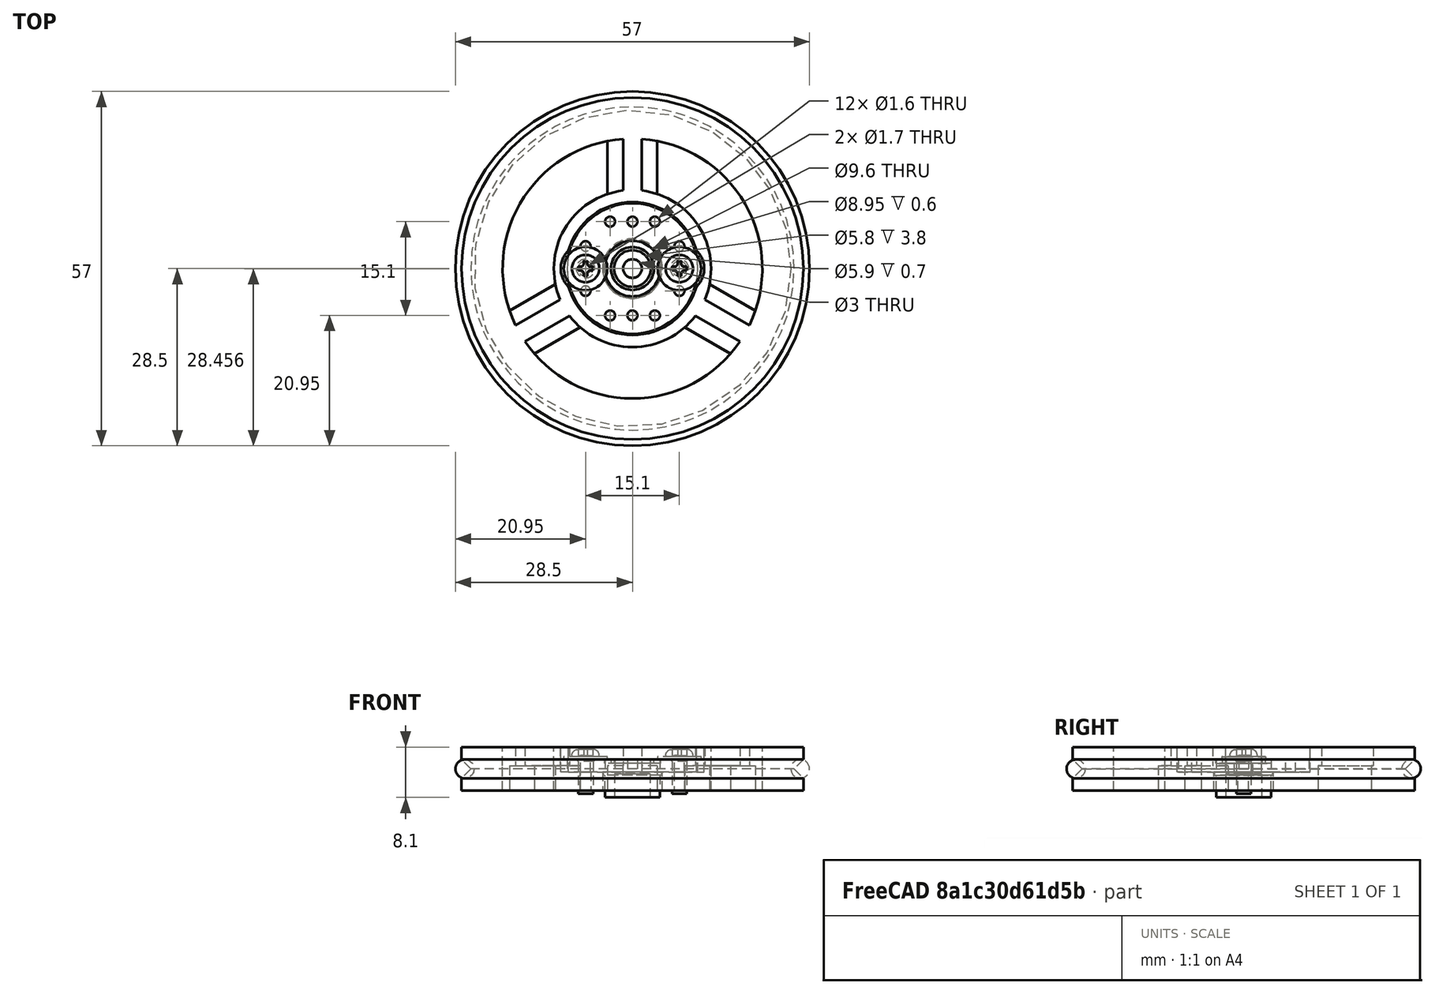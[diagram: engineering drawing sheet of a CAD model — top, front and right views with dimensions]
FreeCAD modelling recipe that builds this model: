
FCSTD DOCUMENT  (FreeCAD 0.14R3702 (Git))
Label: Renacuajo-original-wheel-screws-assembly
License: CC-BY 3.0
LicenseURL: http://creativecommons.org/licenses/by/3.0/
objects: Part::Feature×4, Part::Torus×1, Part::Compound×1
note: 6 computed .brp shape members not serialized (recipe doc carries the construction recipe); baked Part::Feature solids carry a one-line shape summary decoded from their .brp

FEATURE [Part::Feature] Mirrored  label="Renacuajo-original-wheel-screws-final"
  Placement = pos=(0,0,0) rot=(1,0,0;1.5708rad)
  shape: bbox 55 x 55 x 7 mm, 44 faces (baked)
FEATURE [Part::Torus] Torus  label="o-ring"
  Angle1 = -180
  Angle2 = 180
  Angle3 = 360
  Radius1 = 27
  Radius2 = 1.5
FEATURE [Part::Feature] Pocket  label="small-rounded-horn"
  Placement = pos=(0,0,-0.5) rot=(0,0,1;0rad)
  shape: bbox 21 x 21 x 6.2 mm, 28 faces (baked)
FEATURE [Part::Feature] Chamfer  label="screw1"
  Placement = pos=(7.55,0,1.5) rot=(0,0,1;0rad)
  shape: bbox 7 x 7 x 7.14 mm, 33 faces (baked)
FEATURE [Part::Feature] Chamfer001  label="screw2"
  Placement = pos=(-7.55,0,1.5) rot=(0,0,1;0rad)
  shape: bbox 7 x 7 x 7.14 mm, 33 faces (baked)
FEATURE [Part::Compound] Compound  label="Renacuajo-original-wheel-screws-assembly-final"
  Links = -> [Mirrored,Torus,Chamfer001,Pocket,Chamfer]
